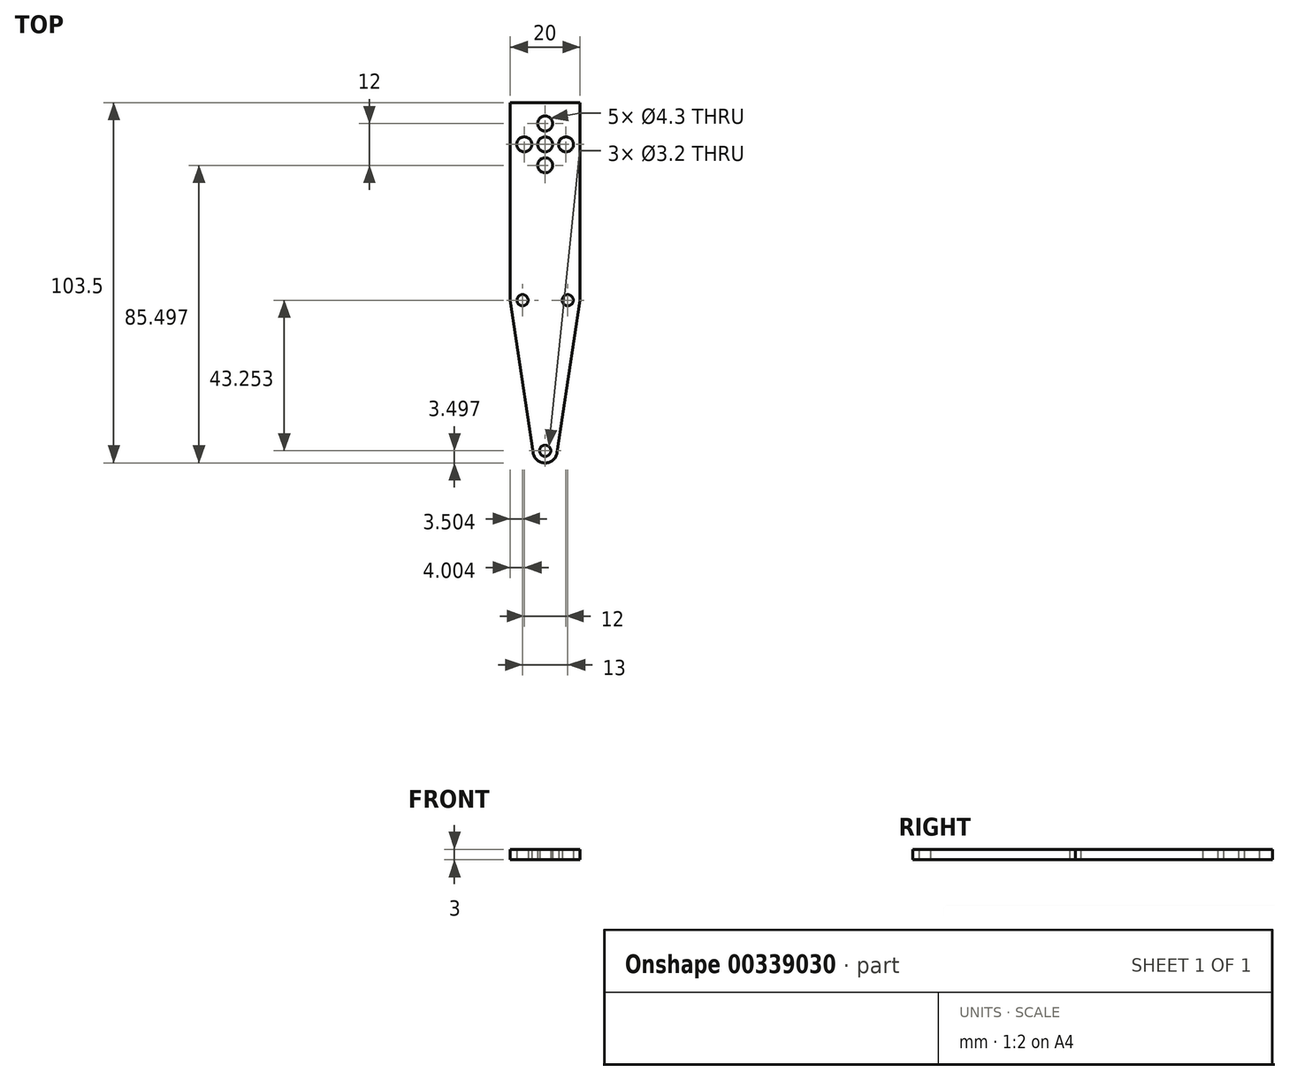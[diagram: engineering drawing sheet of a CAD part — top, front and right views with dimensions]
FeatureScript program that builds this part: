
annotation { "Feature Type Name" : "Feature", "Feature Type Description" : "" }
export const myFeature = defineFeature(function(context is Context, id is Id, definition is map)
    precondition{}
    {
        {
            var Q0;
            Q0=qCreatedBy(makeId("Top.planeOp"),FACE);
            var sketch = newSketch(context, id + "F0", { "sketchPlane" : qUnion([Q0])});
            skCircle(sketch, "E0", {"center": v(10.42, 75.02) * mm, "radius": 2.15 * mm});
            skCircle(sketch, "E1", {"center": v(10.42, 69.02) * mm, "radius": 2.15 * mm});
            skCircle(sketch, "E2", {"center": v(4.42, 75.02) * mm, "radius": 2.15 * mm});
            skCircle(sketch, "E3", {"center": v(10.42, 81.02) * mm, "radius": 2.15 * mm});
            skCircle(sketch, "E4", {"center": v(16.42, 75.02) * mm, "radius": 2.15 * mm});
            skLineSegment(sketch, "E5.bottom", {"start": v(6.81, 87.02) * mm, "end": v(14.03, 87.02) * mm});
            skLineSegment(sketch, "E5.left", {"start": v(0.42, 53.21) * mm, "end": v(0.42, 30.27) * mm});
            skLineSegment(sketch, "E5.right", {"start": v(20.42, 53.21) * mm, "end": v(20.42, 30.27) * mm});
            skArc(sketch, "E6", {"start": v(6.96, -13.5) * mm, "mid": v(10.42, -16.48) * mm, "end": v(13.89, -13.5) * mm});
            skLineSegment(sketch, "E7", {"start": v(0.42, 30.27) * mm, "end": v(6.96, -13.5) * mm});
            skLineSegment(sketch, "E8", {"start": v(20.42, 30.27) * mm, "end": v(13.89, -13.5) * mm});
            skCircle(sketch, "E9", {"center": v(10.42, -12.98) * mm, "radius": 1.6 * mm});
            skCircle(sketch, "E10", {"center": v(3.92, 30.27) * mm, "radius": 1.6 * mm});
            skCircle(sketch, "E11", {"center": v(16.92, 30.27) * mm, "radius": 1.6 * mm});
            skLineSegment(sketch, "E12", {"start": v(20.42, 87.02) * mm, "end": v(0.42, 87.02) * mm});
            skLineSegment(sketch, "E13", {"start": v(0.42, 53.21) * mm, "end": v(0.42, 87.02) * mm});
            skLineSegment(sketch, "E14", {"start": v(20.42, 53.21) * mm, "end": v(20.42, 87.02) * mm});
            skSolve(sketch);
        }
        {
            var Q0;
            Q0=makeQuery(id+"F0.imprint","IMPRINT",FACE,{"disambiguationData":[TD([[makeQuery(id+"F0.imprint","IMPRINT",EDGE,{"derivedFrom":sQuery(id+"F0.wireOp",EDGE,"E0")}),-1.0]])]});
            extrude(context, id + "F1", {"entities" : qUnion([Q0]), "depth" : 3 * mm});
        }
    });
